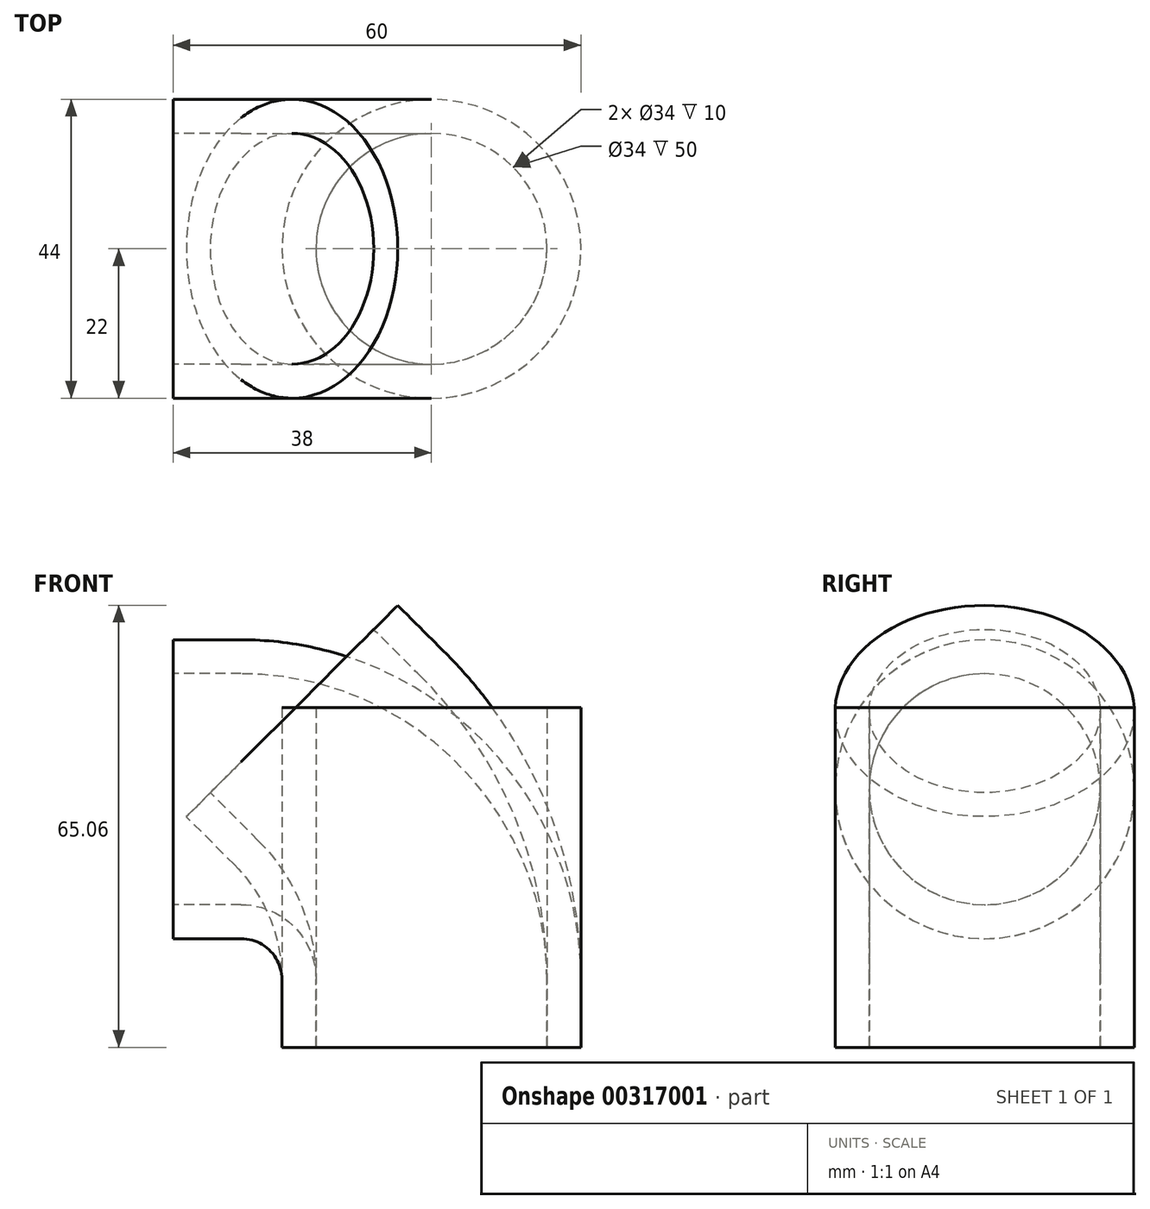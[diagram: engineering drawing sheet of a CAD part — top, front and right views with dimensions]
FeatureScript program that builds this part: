
annotation { "Feature Type Name" : "Feature", "Feature Type Description" : "" }
export const myFeature = defineFeature(function(context is Context, id is Id, definition is map)
    precondition{}
    {
        {
            var Q0;
            Q0=qCreatedBy(makeId("Front.planeOp"),FACE);
            var sketch = newSketch(context, id + "F0", { "sketchPlane" : qUnion([Q0])});
            skLineSegment(sketch, "E0", {"start": v(0, 0) * mm, "end": v(0, 10) * mm});
            skArc(sketch, "E1", {"start": v(0, 10) * mm, "mid": v(-8.2, 29.8) * mm, "end": v(-28, 38) * mm});
            skLineSegment(sketch, "E2", {"start": v(-28, 38) * mm, "end": v(-38, 38) * mm});
            skSolve(sketch);
        }
        {
            var Q0;
            Q0=qCreatedBy(makeId("Top.planeOp"),FACE);
            var sketch = newSketch(context, id + "F1", { "sketchPlane" : qUnion([Q0])});
            skCircle(sketch, "E3", {"center": v(0, 0) * mm, "radius": 22 * mm});
            skCircle(sketch, "E4", {"center": v(0, 0) * mm, "radius": 17 * mm});
            skSolve(sketch);
        }
        {
            var Q0;
            Q0=makeQuery(id+"F1.imprint","IMPRINT",FACE,{"disambiguationData":[TD([[makeQuery(id+"F1.imprint","IMPRINT",EDGE,{"derivedFrom":sQuery(id+"F1.wireOp",EDGE,"E3")}),1.0]])]});
            var Q1;
            Q1 = qConstructionFilter(qBodyType(qCreatedBy(id + "F0" ,EDGE), BodyType.WIRE), ConstructionObject.NO);
            sweep(context, id + "F2", {"profiles" : qUnion([Q0]), "path" : qUnion([Q1])});
        }
        {
            var Q0;
            Q0=qCreatedBy(makeId("Front.planeOp"),FACE);
            var sketch = newSketch(context, id + "F3", { "sketchPlane" : qUnion([Q0])});
            skLineSegment(sketch, "E5", {"start": v(0, 0) * mm, "end": v(0, 10) * mm});
            skArc(sketch, "E6", {"start": v(0, 10) * mm, "mid": v(-3.5, 27.55) * mm, "end": v(-13.44, 42.44) * mm});
            skLineSegment(sketch, "E7", {"start": v(-13.44, 42.44) * mm, "end": v(-20.5, 49.5) * mm});
            skLineSegment(sketch, "E8", {"start": v(-7.78, 62.23) * mm, "end": v(-33.23, 36.78) * mm, "construction": true});
            skLineSegment(sketch, "E9", {"start": v(-13.44, 42.44) * mm, "end": v(0, 29) * mm});
            skLineSegment(sketch, "E10", {"start": v(0, 10) * mm, "end": v(0, 29) * mm});
            skSolve(sketch);
        }
        {
            var Q0;
            Q0=makeQuery(id+"F1.imprint","IMPRINT",FACE,{"disambiguationData":[TD([[makeQuery(id+"F1.imprint","IMPRINT",EDGE,{"derivedFrom":sQuery(id+"F1.wireOp",EDGE,"E3")}),1.0]])]});
            var Q1;
            Q1=sQuery(id+"F3.wireOp",EDGE,"E5");
            var Q2;
            Q2=sQuery(id+"F3.wireOp",EDGE,"E6");
            var Q3;
            Q3=sQuery(id+"F3.wireOp",EDGE,"E7");
            sweep(context, id + "F4", {"profiles" : qUnion([Q0]), "path" : qUnion([Q1, Q2, Q3])});
        }
        {
            var Q0;
            Q0=makeQuery(id+"F1.imprint","IMPRINT",FACE,{"disambiguationData":[TD([[makeQuery(id+"F1.imprint","IMPRINT",EDGE,{"derivedFrom":sQuery(id+"F1.wireOp",EDGE,"E3")}),1.0]])]});
            extrude(context, id + "F5", {"entities" : qUnion([Q0]), "depth" : 50 * mm});
        }
    });
